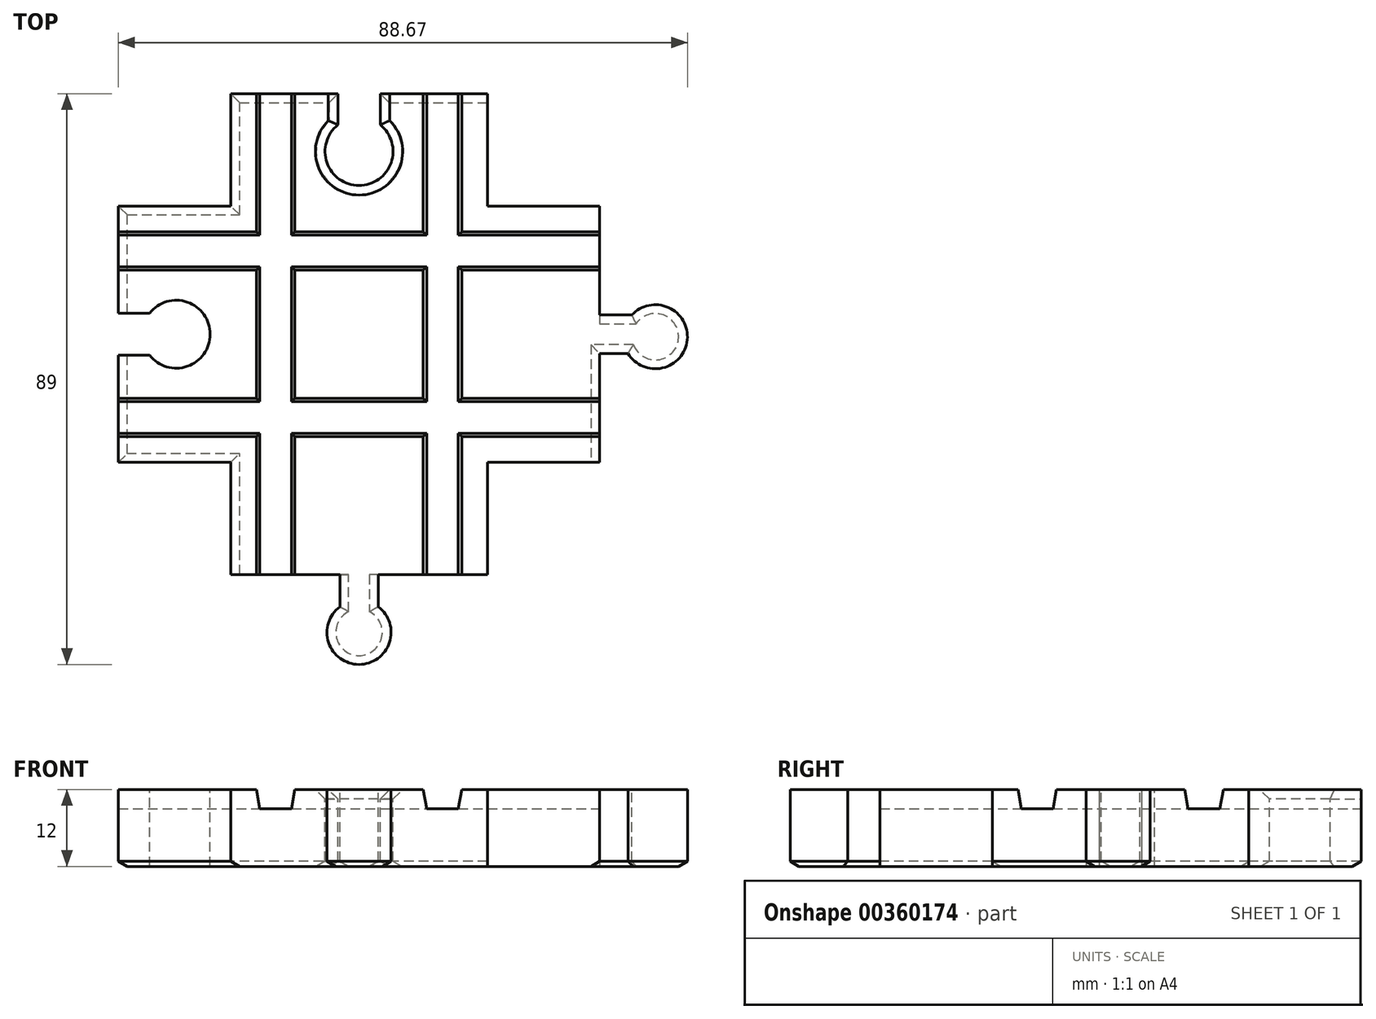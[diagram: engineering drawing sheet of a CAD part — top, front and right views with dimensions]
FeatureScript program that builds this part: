
annotation { "Feature Type Name" : "Feature", "Feature Type Description" : "" }
export const myFeature = defineFeature(function(context is Context, id is Id, definition is map)
    precondition{}
    {
        {
            var Q0;
            Q0=qCreatedBy(makeId("Right.planeOp"),FACE);
            var sketch = newSketch(context, id + "F0", { "sketchPlane" : qUnion([Q0])});
            skLineSegment(sketch, "E0.bottom", {"start": v(20, 0) * mm, "end": v(-20, 0) * mm});
            skLineSegment(sketch, "E0.top", {"start": v(20, 12) * mm, "end": v(-20, 12) * mm});
            skLineSegment(sketch, "E0.left", {"start": v(20, 0) * mm, "end": v(20, 12) * mm});
            skLineSegment(sketch, "E0.right", {"start": v(-20, 0) * mm, "end": v(-20, 12) * mm});
            skSolve(sketch);
        }
        {
            var Q0;
            Q0=makeQuery(id+"F0.imprint","IMPRINT",FACE,{"disambiguationData":[TD([[makeQuery(id+"F0.imprint","IMPRINT",EDGE,{"derivedFrom":sQuery(id+"F0.wireOp",EDGE,"E0.bottom")}),-1.0]])]});
            extrude(context, id + "F1", {"entities" : qUnion([Q0]), "depth" : 75 * mm, "offsetDistance" : 25 * mm});
        }
        {
            var Q0;
            Q0=makeQuery(id+"F1.opExtrude","SWEPT_FACE",FACE,{"disambiguationData":[OSD([sQuery(id+"F0.wireOp",EDGE,"E0.top")])]});
            var sketch = newSketch(context, id + "F2", { "sketchPlane" : qUnion([Q0])});
            skLineSegment(sketch, "E1", {"start": v(37.5, 20) * mm, "end": v(37.5, -20) * mm, "construction": true});
            skLineSegment(sketch, "E2.top", {"start": v(57.5, -37.5) * mm, "end": v(40.5, -37.5) * mm});
            skLineSegment(sketch, "E2.left", {"start": v(57.5, 37.5) * mm, "end": v(57.5, -37.5) * mm});
            skLineSegment(sketch, "E3.left", {"start": v(34.5, -37.5) * mm, "end": v(34.5, -42.5) * mm});
            skLineSegment(sketch, "E3.right", {"start": v(40.5, -37.5) * mm, "end": v(40.5, -42.5) * mm});
            skArc(sketch, "E4", {"start": v(34.5, -42.5) * mm, "mid": v(37.5, -51.5) * mm, "end": v(40.5, -42.5) * mm});
            skLineSegment(sketch, "E5.bottom", {"start": v(75, 3) * mm, "end": v(80, 3) * mm});
            skLineSegment(sketch, "E5.top", {"start": v(75, -3) * mm, "end": v(79.4, -3) * mm});
            skLineSegment(sketch, "E5.left", {"start": v(75, 3) * mm, "end": v(75, -3) * mm});
            skArc(sketch, "E6", {"start": v(79.4, -3) * mm, "mid": v(88.65, -0.89) * mm, "end": v(80, 3) * mm});
            skLineSegment(sketch, "E7.trimOffspring", {"start": v(34.5, -37.5) * mm, "end": v(17.5, -37.5) * mm});
            skPoint(sketch, "E8.right.end.orphan", {"position": v(38.77, 42.04) * mm});
            skPoint(sketch, "E9.orphan", {"position": v(38.77, 32.5) * mm});
            skLineSegment(sketch, "E10.bottom", {"start": v(17.5, -37.5) * mm, "end": v(34.5, -37.5) * mm});
            skLineSegment(sketch, "E10.top", {"start": v(17.5, 37.5) * mm, "end": v(34.5, 37.5) * mm});
            skLineSegment(sketch, "E10.left", {"start": v(17.5, -37.5) * mm, "end": v(17.5, 37.5) * mm});
            skLineSegment(sketch, "E10.right", {"start": v(57.5, -37.5) * mm, "end": v(57.5, 37.5) * mm});
            skLineSegment(sketch, "E11", {"start": v(34.5, 37.5) * mm, "end": v(34.5, 32.5) * mm, "construction": true});
            skArc(sketch, "E12", {"start": v(34.5, 32.5) * mm, "mid": v(37.5, 23.5) * mm, "end": v(40.5, 32.5) * mm, "construction": true});
            skLineSegment(sketch, "E13", {"start": v(40.5, 32.5) * mm, "end": v(40.5, 37.5) * mm, "construction": true});
            skLineSegment(sketch, "E14", {"start": v(40.5, 37.5) * mm, "end": v(40.5, 32.5) * mm});
            skLineSegment(sketch, "E15.trimOffspring", {"start": v(40.5, 37.5) * mm, "end": v(57.5, 37.5) * mm});
            skLineSegment(sketch, "E16.trimOffspring", {"start": v(40.5, -37.5) * mm, "end": v(57.5, -37.5) * mm});
            skLineSegment(sketch, "E17.0", {"start": v(40.8, 32.65) * mm, "end": v(40.8, 37.5) * mm});
            skArc(sketch, "E17.1", {"start": v(34.2, 32.65) * mm, "mid": v(37.5, 23.2) * mm, "end": v(40.8, 32.65) * mm});
            skLineSegment(sketch, "E17.2", {"start": v(34.2, 37.5) * mm, "end": v(34.2, 32.65) * mm});
            skSolve(sketch);
        }
        {
            var Q0;
            Q0=qSketchRegion(id+"F2",true);
            extrude(context, id + "F3", {"entities" : qUnion([Q0]), "operationType" : NewBodyOperationType.ADD, "oppositeDirection" : true, "depth" : 12 * mm, "offsetDistance" : 25 * mm});
        }
        {
            var Q0;
            Q0=makeQuery(id+"F3.boolean.opBoolean","MERGE",FACE,{"derivedFrom":[makeQuery(id+"F1.opExtrude","SWEPT_FACE",FACE,{"disambiguationData":[OSD([sQuery(id+"F0.wireOp",EDGE,"E0.top")])]}),makeQuery(id+"F3.opExtrude","CAP_FACE",FACE,{"disambiguationData":[OSD([sQuery(id+"F2.wireOp",EDGE,"E3.left"),sQuery(id+"F2.wireOp",EDGE,"E3.right"),sQuery(id+"F2.wireOp",EDGE,"E4"),sQuery(id+"F2.wireOp",EDGE,"E10.bottom"),sQuery(id+"F2.wireOp",EDGE,"E10.top"),sQuery(id+"F2.wireOp",EDGE,"E10.left"),sQuery(id+"F2.wireOp",EDGE,"E10.right"),sQuery(id+"F2.wireOp",EDGE,"E15.trimOffspring"),sQuery(id+"F2.wireOp",EDGE,"E16.trimOffspring"),sQuery(id+"F2.wireOp",EDGE,"E17.0"),sQuery(id+"F2.wireOp",EDGE,"E17.1"),sQuery(id+"F2.wireOp",EDGE,"E17.2")])],"isStart":true}),makeQuery(id+"F3.opExtrude","CAP_FACE",FACE,{"disambiguationData":[OSD([sQuery(id+"F2.wireOp",EDGE,"E5.bottom"),sQuery(id+"F2.wireOp",EDGE,"E5.top"),sQuery(id+"F2.wireOp",EDGE,"E5.left"),sQuery(id+"F2.wireOp",EDGE,"E6")])],"isStart":true})]});
            var sketch = newSketch(context, id + "F4", { "sketchPlane" : qUnion([Q0])});
            skLineSegment(sketch, "E18.bottom", {"start": v(0, 3) * mm, "end": v(5, 3) * mm, "construction": true});
            skLineSegment(sketch, "E18.top", {"start": v(0, -3) * mm, "end": v(5, -3) * mm, "construction": true});
            skLineSegment(sketch, "E18.left", {"start": v(0, 3) * mm, "end": v(0, -3) * mm});
            skArc(sketch, "E19", {"start": v(5, -3) * mm, "mid": v(14, 0) * mm, "end": v(5, 3) * mm, "construction": true});
            skLineSegment(sketch, "E20.0", {"start": v(0, -3.3) * mm, "end": v(4.85, -3.3) * mm});
            skArc(sketch, "E20.1", {"start": v(4.85, -3.3) * mm, "mid": v(14.3, 0) * mm, "end": v(4.85, 3.3) * mm});
            skLineSegment(sketch, "E20.2", {"start": v(0, 3.3) * mm, "end": v(4.85, 3.3) * mm});
            skSolve(sketch);
        }
        {
            var Q0;
            {var subQ2=sQuery(id+"F4.wireOp",EDGE,"E18.left");Q0=makeQuery(id+"F4.imprint","IMPRINT",FACE,{"disambiguationData":[TD([[makeQuery(id+"F4.imprint","IMPRINT",EDGE,{"derivedFrom":subQ2}),1.0]])]});}
            extrude(context, id + "F5", {"entities" : qUnion([Q0]), "operationType" : NewBodyOperationType.REMOVE, "oppositeDirection" : true, "depth" : 12 * mm, "offsetDistance" : 25 * mm});
        }
        {
            var Q0;
            {var subQ12=sQuery(id+"F0.wireOp",EDGE,"E0.left");var subQ13=sQuery(id+"F0.wireOp",EDGE,"E0.top");var subQ14=sQuery(id+"F0.wireOp",EDGE,"E0.bottom");Q0=makeQuery(id+"F3.boolean.opBoolean","SPLIT",FACE,{"disambiguationData":[TD([makeQuery(id+"F1.opExtrude","SWEPT_FACE",FACE,{"disambiguationData":[OSD([subQ12])]})])],"derivedFrom":makeQuery(id+"F1.opExtrude","CAP_FACE",FACE,{"disambiguationData":[OSD([subQ14,subQ13,subQ12,sQuery(id+"F0.wireOp",EDGE,"E0.right")])],"isStart":false})});}
            var sketch = newSketch(context, id + "F6", { "sketchPlane" : qUnion([Q0])});
            skLineSegment(sketch, "E21", {"start": v(-16, 12) * mm, "end": v(-15.47, 9) * mm});
            skLineSegment(sketch, "E22", {"start": v(-15.47, 9) * mm, "end": v(-10.53, 9) * mm});
            skLineSegment(sketch, "E23", {"start": v(-10.53, 9) * mm, "end": v(-10, 12) * mm});
            skLineSegment(sketch, "E24", {"start": v(16, 12) * mm, "end": v(15.47, 9) * mm});
            skLineSegment(sketch, "E25", {"start": v(15.47, 9) * mm, "end": v(10.53, 9) * mm});
            skLineSegment(sketch, "E26", {"start": v(10.53, 9) * mm, "end": v(10, 12) * mm});
            skLineSegment(sketch, "E27", {"start": v(-16, 12) * mm, "end": v(-10, 12) * mm});
            skLineSegment(sketch, "E28", {"start": v(10, 12) * mm, "end": v(16, 12) * mm});
            skSolve(sketch);
        }
        {
            var Q0;
            Q0=makeQuery(id+"F6.imprint","IMPRINT",FACE,{"disambiguationData":[TD([[makeQuery(id+"F6.imprint","IMPRINT",EDGE,{"derivedFrom":sQuery(id+"F6.wireOp",EDGE,"E21")}),1.0]])]});
            var Q1;
            Q1=makeQuery(id+"F6.imprint","IMPRINT",FACE,{"disambiguationData":[TD([[makeQuery(id+"F6.imprint","IMPRINT",EDGE,{"derivedFrom":sQuery(id+"F6.wireOp",EDGE,"E24")}),-1.0]])]});
            extrude(context, id + "F7", {"entities" : qUnion([Q0, Q1]), "operationType" : NewBodyOperationType.REMOVE, "oppositeDirection" : true, "depth" : 75 * mm, "offsetDistance" : 25 * mm});
        }
        {
            var Q0;
            Q0=makeQuery(id+"F3.opExtrude","SWEPT_FACE",FACE,{"disambiguationData":[OSD([sQuery(id+"F2.wireOp",EDGE,"E15.trimOffspring")])]});
            var sketch = newSketch(context, id + "F8", { "sketchPlane" : qUnion([Q0])});
            skLineSegment(sketch, "E29", {"start": v(-53.5, 12) * mm, "end": v(-52.97, 9) * mm});
            skLineSegment(sketch, "E30", {"start": v(-52.97, 9) * mm, "end": v(-48.03, 9) * mm});
            skLineSegment(sketch, "E31", {"start": v(-48.03, 9) * mm, "end": v(-47.5, 12) * mm});
            skLineSegment(sketch, "E32", {"start": v(-47.5, 12) * mm, "end": v(-48.03, 9) * mm});
            skLineSegment(sketch, "E33", {"start": v(-53.5, 12) * mm, "end": v(-47.5, 12) * mm});
            skLineSegment(sketch, "E34", {"start": v(-27.5, 12) * mm, "end": v(-26.97, 9) * mm});
            skLineSegment(sketch, "E35", {"start": v(-26.97, 9) * mm, "end": v(-22.03, 9) * mm});
            skLineSegment(sketch, "E36", {"start": v(-22.03, 9) * mm, "end": v(-21.5, 12) * mm});
            skLineSegment(sketch, "E37", {"start": v(-21.5, 12) * mm, "end": v(-27.5, 12) * mm});
            skSolve(sketch);
        }
        {
            var Q0;
            Q0=makeQuery(id+"F8.imprint","IMPRINT",FACE,{"disambiguationData":[TD([[makeQuery(id+"F8.imprint","IMPRINT",EDGE,{"derivedFrom":sQuery(id+"F8.wireOp",EDGE,"E29")}),1.0]])]});
            var Q1;
            Q1=makeQuery(id+"F8.imprint","IMPRINT",FACE,{"disambiguationData":[TD([[makeQuery(id+"F8.imprint","IMPRINT",EDGE,{"derivedFrom":sQuery(id+"F8.wireOp",EDGE,"E34")}),1.0]])]});
            extrude(context, id + "F9", {"entities" : qUnion([Q0, Q1]), "operationType" : NewBodyOperationType.REMOVE, "oppositeDirection" : true, "depth" : 75 * mm, "offsetDistance" : 25 * mm});
        }
        {
            var Q0;
            Q0=makeQuery(id+"F3.opExtrude","CAP_EDGE",EDGE,{"disambiguationData":[OSD([sQuery(id+"F2.wireOp",EDGE,"E4")])],"isStart":false});
            var Q1;
            Q1=makeQuery(id+"F3.opExtrude","CAP_EDGE",EDGE,{"disambiguationData":[OSD([sQuery(id+"F2.wireOp",EDGE,"E3.right")])],"isStart":false});
            var Q2;
            Q2=makeQuery(id+"F3.opExtrude","CAP_EDGE",EDGE,{"disambiguationData":[OSD([sQuery(id+"F2.wireOp",EDGE,"E16.trimOffspring")])],"isStart":false});
            var Q3;
            {var subQ0=sQuery(id+"F0.wireOp",EDGE,"E0.right");var subQ1=sQuery(id+"F0.wireOp",EDGE,"E0.bottom");var subQ2=sQuery(id+"F2.wireOp",EDGE,"E10.right");Q3=makeQuery(id+"F3.boolean.opBoolean","SPLIT",EDGE,{"disambiguationData":[TD([makeQuery(id+"F3.opExtrude","SWEPT_FACE",FACE,{"disambiguationData":[OSD([subQ2])]})])],"derivedFrom":makeQuery(id+"F1.opExtrude","SWEPT_EDGE",EDGE,{"disambiguationData":[OSD([subQ1,subQ0])]})});}
            var Q4;
            Q4=makeQuery(id+"F3.opExtrude","CAP_EDGE",EDGE,{"disambiguationData":[OSD([sQuery(id+"F2.wireOp",EDGE,"E3.left")])],"isStart":false});
            var Q5;
            {var subQ0=sQuery(id+"F0.wireOp",EDGE,"E0.right");var subQ1=sQuery(id+"F0.wireOp",EDGE,"E0.bottom");Q5=makeQuery(id+"F3.boolean.opBoolean","SPLIT",EDGE,{"disambiguationData":[TD([makeQuery(id+"F1.opExtrude","SWEPT_FACE",FACE,{"disambiguationData":[OSD([subQ0])]})])],"derivedFrom":makeQuery(id+"F1.opExtrude","CAP_EDGE",EDGE,{"disambiguationData":[OSD([subQ1])],"isStart":false})});}
            var Q6;
            {var subQ1=sQuery(id+"F2.wireOp",EDGE,"E10.right");Q6=makeQuery(id+"F3.boolean.opBoolean","SPLIT",EDGE,{"disambiguationData":[TD([makeQuery(id+"F1.opExtrude","SWEPT_FACE",FACE,{"disambiguationData":[OSD([sQuery(id+"F0.wireOp",EDGE,"E0.right")])]})])],"derivedFrom":makeQuery(id+"F3.opExtrude","CAP_EDGE",EDGE,{"disambiguationData":[OSD([subQ1])],"isStart":false})});}
            var Q7;
            Q7=makeQuery(id+"F3.opExtrude","CAP_EDGE",EDGE,{"disambiguationData":[OSD([sQuery(id+"F2.wireOp",EDGE,"E5.bottom")])],"isStart":false});
            var Q8;
            Q8=makeQuery(id+"F3.opExtrude","CAP_EDGE",EDGE,{"disambiguationData":[OSD([sQuery(id+"F2.wireOp",EDGE,"E5.top")])],"isStart":false});
            var Q9;
            Q9=makeQuery(id+"F3.opExtrude","CAP_EDGE",EDGE,{"disambiguationData":[OSD([sQuery(id+"F2.wireOp",EDGE,"E6")])],"isStart":false});
            var Q10;
            {var subQ0=sQuery(id+"F0.wireOp",EDGE,"E0.left");var subQ1=sQuery(id+"F2.wireOp",EDGE,"E10.right");var subQ2=sQuery(id+"F0.wireOp",EDGE,"E0.bottom");Q10=makeQuery(id+"F3.boolean.opBoolean","SPLIT",EDGE,{"disambiguationData":[TD([makeQuery(id+"F3.opExtrude","SWEPT_FACE",FACE,{"disambiguationData":[OSD([subQ1])]})])],"derivedFrom":makeQuery(id+"F1.opExtrude","SWEPT_EDGE",EDGE,{"disambiguationData":[OSD([subQ2,subQ0])]})});}
            var Q11;
            {var subQ0=sQuery(id+"F2.wireOp",EDGE,"E10.right");Q11=makeQuery(id+"F3.boolean.opBoolean","SPLIT",EDGE,{"disambiguationData":[TD([makeQuery(id+"F1.opExtrude","SWEPT_FACE",FACE,{"disambiguationData":[OSD([sQuery(id+"F0.wireOp",EDGE,"E0.left")])]})])],"derivedFrom":makeQuery(id+"F3.opExtrude","CAP_EDGE",EDGE,{"disambiguationData":[OSD([subQ0])],"isStart":false})});}
            var Q12;
            Q12=makeQuery(id+"F3.opExtrude","CAP_EDGE",EDGE,{"disambiguationData":[OSD([sQuery(id+"F2.wireOp",EDGE,"E15.trimOffspring")])],"isStart":false});
            var Q13;
            Q13=makeQuery(id+"F3.opExtrude","CAP_EDGE",EDGE,{"disambiguationData":[OSD([sQuery(id+"F2.wireOp",EDGE,"E17.0")])],"isStart":false});
            var Q14;
            Q14=makeQuery(id+"F3.opExtrude","CAP_EDGE",EDGE,{"disambiguationData":[OSD([sQuery(id+"F2.wireOp",EDGE,"E17.1")])],"isStart":false});
            var Q15;
            Q15=makeQuery(id+"F3.opExtrude","CAP_EDGE",EDGE,{"disambiguationData":[OSD([sQuery(id+"F2.wireOp",EDGE,"E17.2")])],"isStart":false});
            var Q16;
            Q16=makeQuery(id+"F3.opExtrude","CAP_EDGE",EDGE,{"disambiguationData":[OSD([sQuery(id+"F2.wireOp",EDGE,"E10.top")])],"isStart":false});
            var Q17;
            {var subQ0=sQuery(id+"F2.wireOp",EDGE,"E10.left");Q17=makeQuery(id+"F3.boolean.opBoolean","SPLIT",EDGE,{"disambiguationData":[TD([makeQuery(id+"F1.opExtrude","SWEPT_FACE",FACE,{"disambiguationData":[OSD([sQuery(id+"F0.wireOp",EDGE,"E0.left")])]})])],"derivedFrom":makeQuery(id+"F3.opExtrude","CAP_EDGE",EDGE,{"disambiguationData":[OSD([subQ0])],"isStart":false})});}
            var Q18;
            {var subQ0=sQuery(id+"F0.wireOp",EDGE,"E0.left");var subQ1=sQuery(id+"F0.wireOp",EDGE,"E0.bottom");var subQ2=sQuery(id+"F2.wireOp",EDGE,"E10.left");Q18=makeQuery(id+"F3.boolean.opBoolean","SPLIT",EDGE,{"disambiguationData":[TD([makeQuery(id+"F3.opExtrude","SWEPT_FACE",FACE,{"disambiguationData":[OSD([subQ2])]})])],"derivedFrom":makeQuery(id+"F1.opExtrude","SWEPT_EDGE",EDGE,{"disambiguationData":[OSD([subQ1,subQ0])]})});}
            var Q19;
            Q19=makeQuery(id+"F5.boolean.opBoolean","COPY",EDGE,{"derivedFrom":makeQuery(id+"F5.opExtrude","CAP_EDGE",EDGE,{"disambiguationData":[OSD([sQuery(id+"F4.wireOp",EDGE,"E20.0")])],"isStart":false})});
            var Q20;
            Q20=makeQuery(id+"F5.boolean.opBoolean","COPY",EDGE,{"derivedFrom":makeQuery(id+"F5.opExtrude","CAP_EDGE",EDGE,{"disambiguationData":[OSD([sQuery(id+"F4.wireOp",EDGE,"E20.1")])],"isStart":false})});
            var Q21;
            Q21=makeQuery(id+"F5.boolean.opBoolean","COPY",EDGE,{"derivedFrom":makeQuery(id+"F5.opExtrude","CAP_EDGE",EDGE,{"disambiguationData":[OSD([sQuery(id+"F4.wireOp",EDGE,"E20.2")])],"isStart":false})});
            var Q22;
            {var subQ0=sQuery(id+"F0.wireOp",EDGE,"E0.left");var subQ1=sQuery(id+"F0.wireOp",EDGE,"E0.bottom");Q22=makeQuery(id+"F5.boolean.opBoolean","SPLIT",EDGE,{"disambiguationData":[TD([makeQuery(id+"F1.opExtrude","SWEPT_FACE",FACE,{"disambiguationData":[OSD([subQ0])]})])],"derivedFrom":makeQuery(id+"F1.opExtrude","CAP_EDGE",EDGE,{"disambiguationData":[OSD([subQ1])],"isStart":true})});}
            var Q23;
            {var subQ0=sQuery(id+"F0.wireOp",EDGE,"E0.right");var subQ1=sQuery(id+"F0.wireOp",EDGE,"E0.bottom");Q23=makeQuery(id+"F5.boolean.opBoolean","SPLIT",EDGE,{"disambiguationData":[TD([makeQuery(id+"F1.opExtrude","SWEPT_FACE",FACE,{"disambiguationData":[OSD([subQ0])]})])],"derivedFrom":makeQuery(id+"F1.opExtrude","CAP_EDGE",EDGE,{"disambiguationData":[OSD([subQ1])],"isStart":true})});}
            var Q24;
            {var subQ0=sQuery(id+"F0.wireOp",EDGE,"E0.right");var subQ1=sQuery(id+"F0.wireOp",EDGE,"E0.bottom");var subQ2=sQuery(id+"F2.wireOp",EDGE,"E10.left");Q24=makeQuery(id+"F3.boolean.opBoolean","SPLIT",EDGE,{"disambiguationData":[TD([makeQuery(id+"F3.opExtrude","SWEPT_FACE",FACE,{"disambiguationData":[OSD([subQ2])]})])],"derivedFrom":makeQuery(id+"F1.opExtrude","SWEPT_EDGE",EDGE,{"disambiguationData":[OSD([subQ1,subQ0])]})});}
            var Q25;
            {var subQ0=sQuery(id+"F2.wireOp",EDGE,"E10.left");Q25=makeQuery(id+"F3.boolean.opBoolean","SPLIT",EDGE,{"disambiguationData":[TD([makeQuery(id+"F1.opExtrude","SWEPT_FACE",FACE,{"disambiguationData":[OSD([sQuery(id+"F0.wireOp",EDGE,"E0.right")])]})])],"derivedFrom":makeQuery(id+"F3.opExtrude","CAP_EDGE",EDGE,{"disambiguationData":[OSD([subQ0])],"isStart":false})});}
            var Q26;
            Q26=makeQuery(id+"F3.opExtrude","CAP_EDGE",EDGE,{"disambiguationData":[OSD([sQuery(id+"F2.wireOp",EDGE,"E10.bottom")])],"isStart":false});
            chamfer(context, id + "F10", {"entities" : qUnion([Q0, Q1, Q2, Q3, Q4, Q5, Q6, Q7, Q8, Q9, Q10, Q11, Q12, Q13, Q14, Q15, Q16, Q17, Q18, Q19, Q20, Q21, Q22, Q23, Q24, Q25, Q26]), "chamferType" : ChamferType.OFFSET_ANGLE, "width" : 0.8 * mm, "oppositeDirection" : false, "angle" : 60 * degree, "tangentPropagation" : true});
        }
        {
            var Q0;
            Q0=makeQuery(id+"F5.boolean.opBoolean","COPY",EDGE,{"derivedFrom":makeQuery(id+"F5.opExtrude","CAP_EDGE",EDGE,{"disambiguationData":[OSD([sQuery(id+"F4.wireOp",EDGE,"E20.0")])],"isStart":true})});
            var Q1;
            Q1=makeQuery(id+"F5.boolean.opBoolean","COPY",EDGE,{"derivedFrom":makeQuery(id+"F5.opExtrude","CAP_EDGE",EDGE,{"disambiguationData":[OSD([sQuery(id+"F4.wireOp",EDGE,"E20.1")])],"isStart":true})});
            var Q2;
            Q2=makeQuery(id+"F5.boolean.opBoolean","COPY",EDGE,{"derivedFrom":makeQuery(id+"F5.opExtrude","CAP_EDGE",EDGE,{"disambiguationData":[OSD([sQuery(id+"F4.wireOp",EDGE,"E20.2")])],"isStart":true})});
            var Q3;
            Q3=makeQuery(id+"F3.opExtrude","CAP_EDGE",EDGE,{"disambiguationData":[OSD([sQuery(id+"F2.wireOp",EDGE,"E17.1")])],"isStart":true});
            var Q4;
            Q4=makeQuery(id+"F3.opExtrude","CAP_EDGE",EDGE,{"disambiguationData":[OSD([sQuery(id+"F2.wireOp",EDGE,"E17.2")])],"isStart":true});
            var Q5;
            Q5=makeQuery(id+"F3.opExtrude","CAP_EDGE",EDGE,{"disambiguationData":[OSD([sQuery(id+"F2.wireOp",EDGE,"E17.0")])],"isStart":true});
            chamfer(context, id + "F11", {"entities" : qUnion([Q0, Q1, Q2, Q3, Q4, Q5]), "width" : 1.5 * mm, "tangentPropagation" : true});
        }
    });
